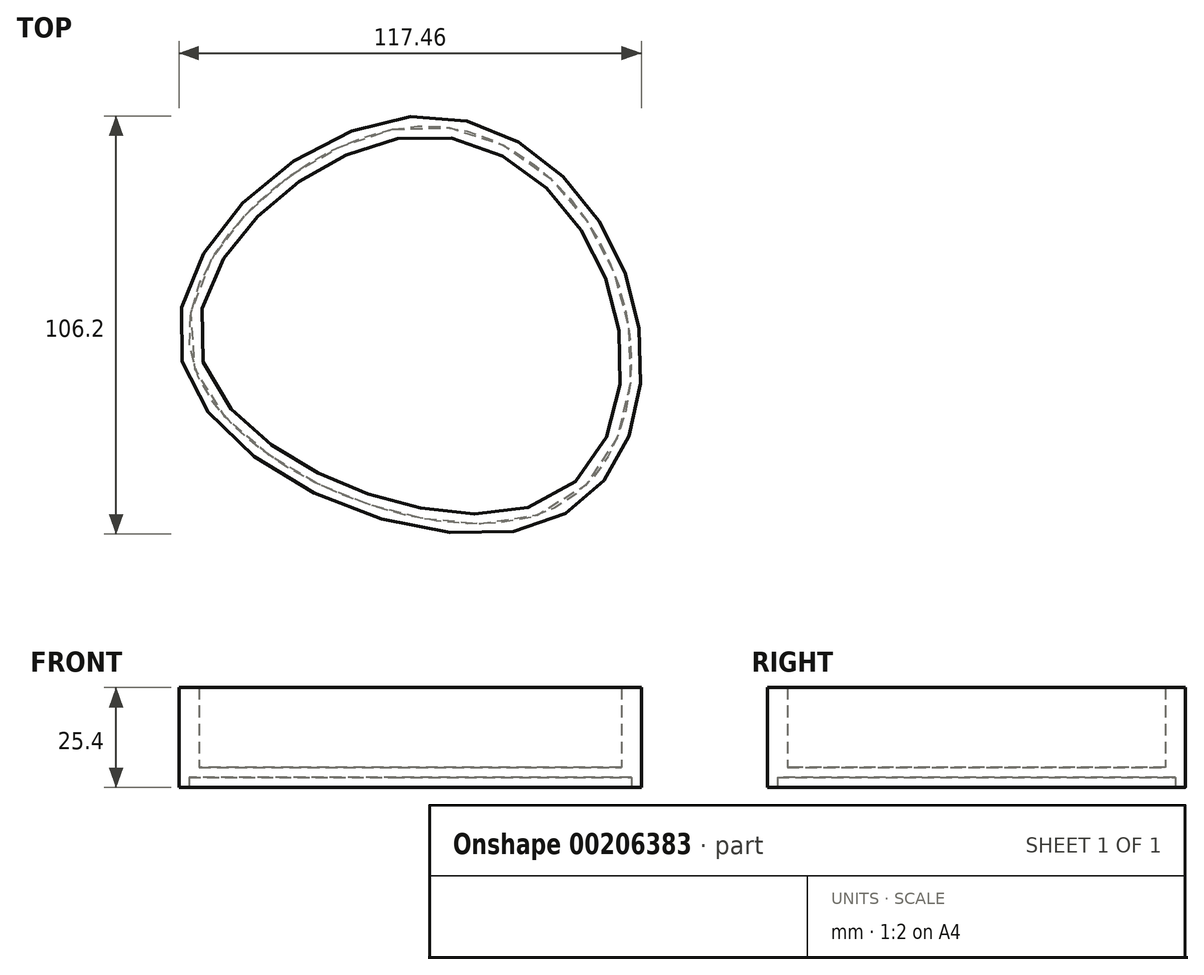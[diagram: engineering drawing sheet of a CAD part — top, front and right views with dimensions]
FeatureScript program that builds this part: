
annotation { "Feature Type Name" : "Feature", "Feature Type Description" : "" }
export const myFeature = defineFeature(function(context is Context, id is Id, definition is map)
    precondition{}
    {
        {
            var Q0;
            Q0=qCreatedBy(makeId("Top.planeOp"),FACE);
            var sketch = newSketch(context, id + "F0", { "sketchPlane" : qUnion([Q0])});
            skFitSpline(sketch, "E0", {"points": [v(-10.42, 61.31) * mm, v(46.29, 14.1) * mm, v(20.85, -42.92) * mm, v(-68.67, 0) * mm, v(-10.42, 61.31) * mm]});
            skSolve(sketch);
        }
        {
            var Q0;
            Q0=makeQuery(id+"F0.imprint","IMPRINT",FACE,{"disambiguationData":[TD([[makeQuery(id+"F0.imprint","IMPRINT",EDGE,{"derivedFrom":sQuery(id+"F0.wireOp",EDGE,"E0")}),-1.0]])]});
            extrude(context, id + "F1", {"entities" : qUnion([Q0]), "depth" : 25.4 * mm});
        }
        {
            var Q0;
            Q0=makeQuery(id+"F1.opExtrude","CAP_FACE",FACE,{"disambiguationData":[OSD([sQuery(id+"F0.wireOp",EDGE,"E0")])],"isStart":false});
            shell(context, id + "F2", {"entities" : qUnion([Q0]), "thickness" : 5.08 * mm});
        }
        {
            var Q0;
            Q0=makeQuery(id+"F1.opExtrude","CAP_FACE",FACE,{"disambiguationData":[OSD([sQuery(id+"F0.wireOp",EDGE,"E0")])],"isStart":true});
            shell(context, id + "F3", {"entities" : qUnion([Q0]), "thickness" : 2.54 * mm});
        }
    });
